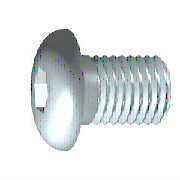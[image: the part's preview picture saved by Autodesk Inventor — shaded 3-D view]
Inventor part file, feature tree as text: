
AUTODESK INVENTOR PART (.ipt)
format: ipt  version: 2013 (Build 170138000, 138)  size: 187,904 bytes
history: native  units: mm (DEFAULTED — no unit token found)
features: sketch x2, extrude x1, plane x1
ambient origin geometry x7: Origin, YZ Plane, XY Plane, X Axis, Y Axis, Z Axis, Center Point
bodies: Solid1 (feature_tree), Body (feature_tree)
feature tree (4):
  extrude  "Slot"  Depth=0.49076mm
  plane  "Work Plane1"
  sketch  "Sketch1"  dims[d0=23.4mm d1=0.49076mm]
  sketch  "Sketch2"  dims[d2=2.75mm d3=1.56mm d4=60.0deg d5=5.0mm d6=5.0mm d7=3.464102mm d8=9.5mm d10=90.0deg d11=10.0mm d9=0.0mm d12=23.4mm d13=0.0mm d14=0.49076mm d15=0.49076mm d16=2.375mm d17=0.0mm d18=0.0mm d19=25.0mm d27=45.0deg d28=0.2mm d29=0.2mm]
